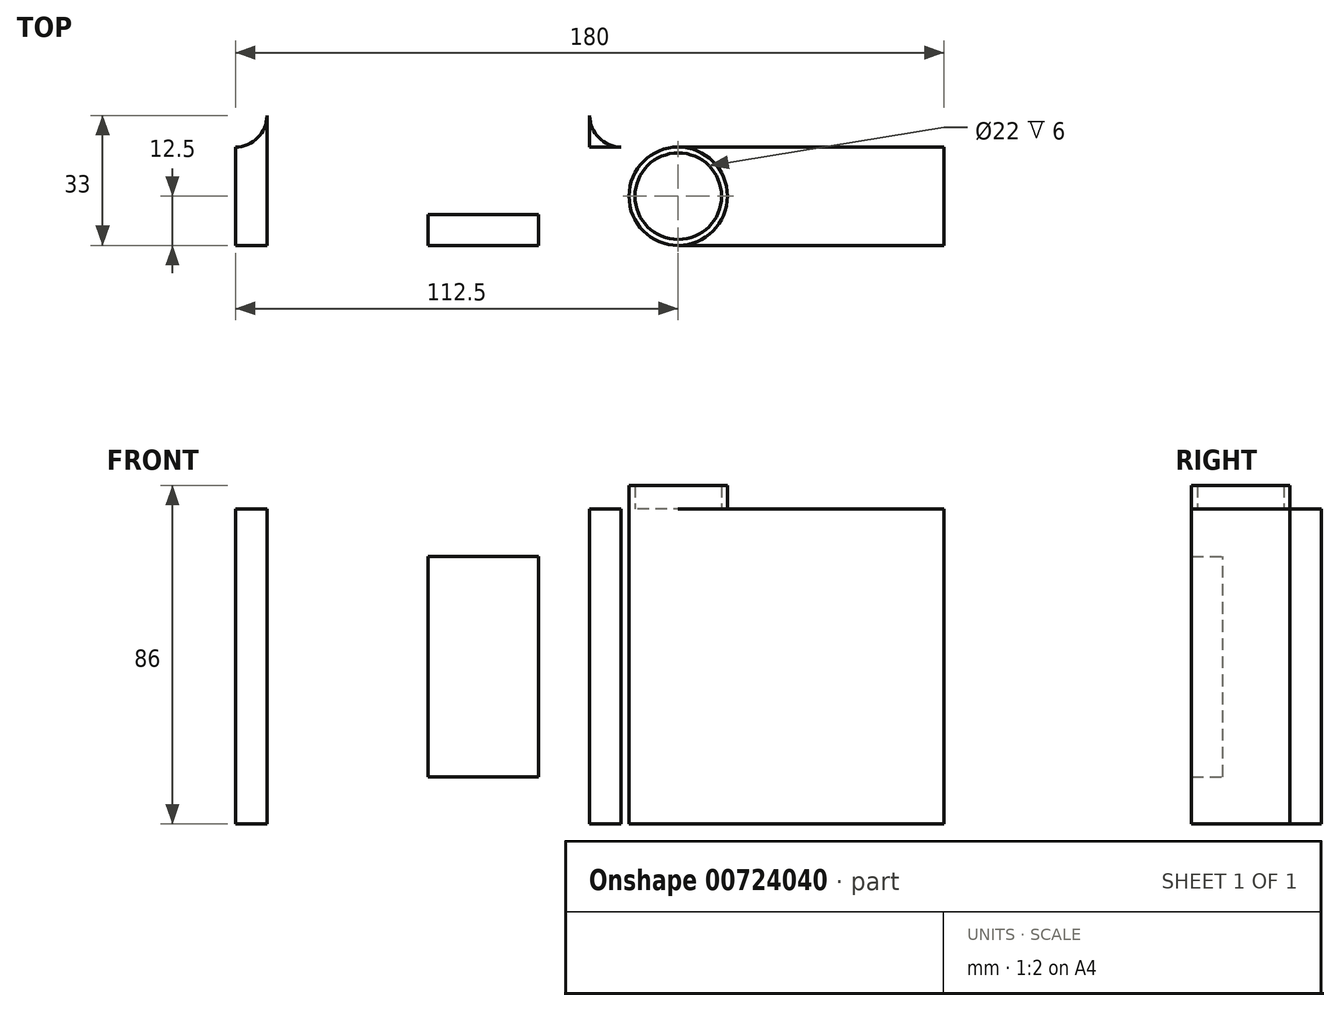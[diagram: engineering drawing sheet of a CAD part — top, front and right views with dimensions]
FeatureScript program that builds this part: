
annotation { "Feature Type Name" : "Feature", "Feature Type Description" : "" }
export const myFeature = defineFeature(function(context is Context, id is Id, definition is map)
    precondition{}
    {
        {
            var Q0;
            Q0=qCreatedBy(makeId("Top.planeOp"),FACE);
            var sketch = newSketch(context, id + "F0", { "sketchPlane" : qUnion([Q0])});
            skLineSegment(sketch, "E0", {"start": v(0, 0) * mm, "end": v(41, 0) * mm});
            skLineSegment(sketch, "E1", {"start": v(0, 0) * mm, "end": v(-49, 0) * mm});
            skLineSegment(sketch, "E2", {"start": v(-49, 0) * mm, "end": v(-49, -15) * mm});
            skLineSegment(sketch, "E3", {"start": v(-49, 0) * mm, "end": v(-49, 19.9) * mm});
            skLineSegment(sketch, "E4", {"start": v(-49, 19.9) * mm, "end": v(0, 19.9) * mm});
            skLineSegment(sketch, "E5", {"start": v(0, 19.9) * mm, "end": v(41, 19.9) * mm});
            skLineSegment(sketch, "E6", {"start": v(41, 19.9) * mm, "end": v(41, 18) * mm});
            skLineSegment(sketch, "E7", {"start": v(-49, -15) * mm, "end": v(0, -15) * mm});
            skLineSegment(sketch, "E8", {"start": v(0, -15) * mm, "end": v(41, -15) * mm});
            skLineSegment(sketch, "E9", {"start": v(41, -15) * mm, "end": v(41, 0) * mm});
            skLineSegment(sketch, "E10", {"start": v(41, -15) * mm, "end": v(131, -15) * mm});
            skLineSegment(sketch, "E11", {"start": v(41, -15) * mm, "end": v(41, 10) * mm});
            skLineSegment(sketch, "E12", {"start": v(41, 10) * mm, "end": v(131, 10) * mm});
            skLineSegment(sketch, "E13", {"start": v(131, 10) * mm, "end": v(131, -15) * mm});
            skLineSegment(sketch, "E14", {"start": v(42.9, 10) * mm, "end": v(41, 10) * mm});
            skLineSegment(sketch, "E15", {"start": v(-49, 19.9) * mm, "end": v(-49, 9.95) * mm});
            skLineSegment(sketch, "E16", {"start": v(-49, 19.9) * mm, "end": v(-49, 10) * mm});
            skLineSegment(sketch, "E17", {"start": v(-49, 10) * mm, "end": v(-49, 10) * mm});
            skLineSegment(sketch, "E18", {"start": v(-41, 18) * mm, "end": v(-41, 19.9) * mm});
            skLineSegment(sketch, "E19", {"start": v(24, 19.9) * mm, "end": v(24, 19.9) * mm});
            skPoint(sketch, "E20.visualSharp", {"position": v(-41, 10) * mm});
            skArc(sketch, "E20.filletArc", {"start": v(-49, 10) * mm, "mid": v(-43.34, 12.34) * mm, "end": v(-41, 18) * mm});
            skLineSegment(sketch, "E21", {"start": v(41, -15) * mm, "end": v(86, -15) * mm});
            skLineSegment(sketch, "E22", {"start": v(86, -15) * mm, "end": v(86, 10) * mm});
            skLineSegment(sketch, "E23", {"start": v(86, 10) * mm, "end": v(86, -2.5) * mm});
            skLineSegment(sketch, "E24", {"start": v(41, -15) * mm, "end": v(63.5, -15) * mm});
            skLineSegment(sketch, "E25", {"start": v(63.5, -15) * mm, "end": v(63.5, 10) * mm});
            skLineSegment(sketch, "E26", {"start": v(63.5, 10) * mm, "end": v(63.5, -2.5) * mm});
            skCircle(sketch, "E27", {"center": v(63.5, -2.5) * mm, "radius": 12.5 * mm});
            skCircle(sketch, "E28", {"center": v(63.5, -2.5) * mm, "radius": 11 * mm});
            skLineSegment(sketch, "E29", {"start": v(49, 10) * mm, "end": v(49, 10) * mm});
            skPoint(sketch, "E30.newPointA", {"position": v(41, 10) * mm});
            skArc(sketch, "E30.filletArc", {"start": v(41, 18) * mm, "mid": v(43.34, 12.34) * mm, "end": v(49, 10) * mm});
            skSolve(sketch);
        }
        {
            var Q0;
            {var subQ13=sQuery(id+"F0.wireOp",EDGE,"E0");Q0=makeQuery(id+"F0.imprint","IMPRINT",FACE,{"disambiguationData":[TD([[makeQuery(id+"F0.imprint","IMPRINT",EDGE,{"derivedFrom":subQ13}),1.0]])]});}
            var Q1;
            {var subQ1=sQuery(id+"F0.wireOp",EDGE,"E0");Q1=makeQuery(id+"F0.imprint","IMPRINT",FACE,{"disambiguationData":[TD([[makeQuery(id+"F0.imprint","IMPRINT",EDGE,{"derivedFrom":subQ1}),-1.0]])]});}
            var Q2;
            {var subQ0=sQuery(id+"F0.wireOp",EDGE,"E14");Q2=makeQuery(id+"F0.imprint","IMPRINT",FACE,{"disambiguationData":[TD([[makeQuery(id+"F0.imprint","IMPRINT",EDGE,{"derivedFrom":subQ0}),1.0]])]});}
            var Q3;
            {var subQ1=sQuery(id+"F0.wireOp",EDGE,"E21");Q3=makeQuery(id+"F0.imprint","IMPRINT",FACE,{"disambiguationData":[TD([[makeQuery(id+"F0.imprint","IMPRINT",EDGE,{"derivedFrom":subQ1}),1.0]])]});}
            var Q4;
            Q4=makeQuery(id+"F0.imprint","IMPRINT",FACE,{"disambiguationData":[TD([[makeQuery(id+"F0.imprint","IMPRINT",EDGE,{"derivedFrom":sQuery(id+"F0.wireOp",EDGE,"E10")}),1.0]])]});
            var Q5;
            {var subQ0=sQuery(id+"F0.wireOp",EDGE,"E26");var subQ1=sQuery(id+"F0.wireOp",EDGE,"E25");var subQ2=makeQuery(id+"F0.imprint","INTERSECT",VERTEX,{"derivedFrom":[subQ1,subQ0]});Q5=makeQuery(id+"F0.imprint","IMPRINT",FACE,{"disambiguationData":[TD([[makeQuery(id+"F0.imprint","IMPRINT",EDGE,{"disambiguationData":[TD([[subQ2,1.0]])],"derivedFrom":subQ1}),-1.0]])]});}
            var Q6;
            {var subQ0=sQuery(id+"F0.wireOp",EDGE,"E26");var subQ1=sQuery(id+"F0.wireOp",EDGE,"E25");var subQ2=makeQuery(id+"F0.imprint","INTERSECT",VERTEX,{"derivedFrom":[subQ1,subQ0]});Q6=makeQuery(id+"F0.imprint","IMPRINT",FACE,{"disambiguationData":[TD([[makeQuery(id+"F0.imprint","IMPRINT",EDGE,{"disambiguationData":[TD([[subQ2,1.0]])],"derivedFrom":subQ1}),1.0]])]});}
            var Q7;
            {var subQ1=sQuery(id+"F0.wireOp",EDGE,"E25");var subQ3=sQuery(id+"F0.wireOp",EDGE,"E28");var subQ4=makeQuery(id+"F0.imprint","INTERSECT",VERTEX,{"derivedFrom":[subQ1,subQ3]});Q7=makeQuery(id+"F0.imprint","IMPRINT",FACE,{"disambiguationData":[TD([[makeQuery(id+"F0.imprint","IMPRINT",EDGE,{"disambiguationData":[TD([[subQ4,1.0]])],"derivedFrom":subQ3}),-1.0]])]});}
            var Q8;
            {var subQ1=sQuery(id+"F0.wireOp",EDGE,"E25");var subQ3=sQuery(id+"F0.wireOp",EDGE,"E28");var subQ4=makeQuery(id+"F0.imprint","INTERSECT",VERTEX,{"derivedFrom":[subQ1,subQ3]});Q8=makeQuery(id+"F0.imprint","IMPRINT",FACE,{"disambiguationData":[TD([[makeQuery(id+"F0.imprint","IMPRINT",EDGE,{"disambiguationData":[TD([[subQ4,-1.0]])],"derivedFrom":subQ3}),-1.0]])]});}
            extrude(context, id + "F1", {"entities" : qUnion([Q0, Q1, Q2, Q3, Q4, Q5, Q6, Q7, Q8]), "endBound" : BoundingType.SYMMETRIC, "depth" : 80 * mm, "offsetDistance" : 25 * mm});
        }
        {
            var Q0;
            {var subQ1=sQuery(id+"F0.wireOp",EDGE,"E25");var subQ3=sQuery(id+"F0.wireOp",EDGE,"E28");var subQ4=makeQuery(id+"F0.imprint","INTERSECT",VERTEX,{"derivedFrom":[subQ1,subQ3]});Q0=makeQuery(id+"F0.imprint","IMPRINT",FACE,{"disambiguationData":[TD([[makeQuery(id+"F0.imprint","IMPRINT",EDGE,{"disambiguationData":[TD([[subQ4,1.0]])],"derivedFrom":subQ3}),-1.0]])]});}
            var Q1;
            {var subQ1=sQuery(id+"F0.wireOp",EDGE,"E25");var subQ3=sQuery(id+"F0.wireOp",EDGE,"E28");var subQ4=makeQuery(id+"F0.imprint","INTERSECT",VERTEX,{"derivedFrom":[subQ1,subQ3]});Q1=makeQuery(id+"F0.imprint","IMPRINT",FACE,{"disambiguationData":[TD([[makeQuery(id+"F0.imprint","IMPRINT",EDGE,{"disambiguationData":[TD([[subQ4,-1.0]])],"derivedFrom":subQ3}),-1.0]])]});}
            extrude(context, id + "F2", {"entities" : qUnion([Q0, Q1]), "operationType" : NewBodyOperationType.ADD, "depth" : 46 * mm, "offsetDistance" : 25 * mm});
        }
        {
            var Q0;
            Q0=makeQuery(id+"F1.opExtrude","SWEPT_FACE",FACE,{"disambiguationData":[OSD([sQuery(id+"F0.wireOp",EDGE,"E4"),sQuery(id+"F0.wireOp",EDGE,"E5"),sQuery(id+"F0.wireOp",EDGE,"xz5f9xwi-Rsmr-XxTJ-q0zS-7Ez9dwEFxO9i"),sQuery(id+"F0.wireOp",EDGE,"bfca25d2-a378-4aca-a1b2-c8aff88f09880.MirrorCS")])]});
            var sketch = newSketch(context, id + "F3", { "sketchPlane" : qUnion([Q0])});
            skLineSegment(sketch, "E31", {"start": v(0, 0) * mm, "end": v(30, 0) * mm});
            skLineSegment(sketch, "E32", {"start": v(0, 0) * mm, "end": v(-33, 0) * mm});
            skPoint(sketch, "E32.endSnap0", {"position": v(-41, 0) * mm});
            skLineSegment(sketch, "E33", {"start": v(0, 0) * mm, "end": v(0, 33) * mm});
            skPoint(sketch, "E33.endSnap0", {"position": v(0, 40) * mm});
            skLineSegment(sketch, "E34", {"start": v(0, 0) * mm, "end": v(0, -30) * mm});
            skLineSegment(sketch, "E35", {"start": v(-33, 0) * mm, "end": v(-33, 33) * mm});
            skLineSegment(sketch, "E36", {"start": v(-33, 33) * mm, "end": v(0, 33) * mm});
            skLineSegment(sketch, "E37.MirrorCS", {"start": v(33, 33) * mm, "end": v(0, 33) * mm});
            skLineSegment(sketch, "E38.MirrorCS", {"start": v(33, 0) * mm, "end": v(33, 33) * mm});
            skLineSegment(sketch, "E39.MirrorCS", {"start": v(-33, 0) * mm, "end": v(-33, -33) * mm});
            skLineSegment(sketch, "E40.MirrorCS", {"start": v(-33, -33) * mm, "end": v(0, -33) * mm});
            skLineSegment(sketch, "E41.MirrorCS", {"start": v(33, -33) * mm, "end": v(0, -33) * mm});
            skLineSegment(sketch, "E42.MirrorCS", {"start": v(33, 0) * mm, "end": v(33, -33) * mm});
            skLineSegment(sketch, "E43", {"start": v(0, 0) * mm, "end": v(-28, 0) * mm});
            skLineSegment(sketch, "E44", {"start": v(0, 0) * mm, "end": v(0, 28) * mm});
            skLineSegment(sketch, "E45", {"start": v(-28, 0) * mm, "end": v(-28, 28) * mm});
            skLineSegment(sketch, "E46", {"start": v(-28, 28) * mm, "end": v(0, 28) * mm});
            skLineSegment(sketch, "E47.MirrorCS", {"start": v(28, 0) * mm, "end": v(28, 28) * mm});
            skLineSegment(sketch, "E48.MirrorCS", {"start": v(28, 28) * mm, "end": v(0, 28) * mm});
            skLineSegment(sketch, "E49.MirrorCS", {"start": v(-28, -28) * mm, "end": v(0, -28) * mm});
            skLineSegment(sketch, "E50.MirrorCS", {"start": v(-28, 0) * mm, "end": v(-28, -28) * mm});
            skLineSegment(sketch, "E51.MirrorCS", {"start": v(28, -28) * mm, "end": v(0, -28) * mm});
            skLineSegment(sketch, "E52.MirrorCS", {"start": v(28, 0) * mm, "end": v(28, -28) * mm});
            skSolve(sketch);
        }
        {
            var Q0;
            Q0=makeQuery(id+"F3.imprint","IMPRINT",FACE,{"disambiguationData":[TD([[makeQuery(id+"F3.imprint","IMPRINT",EDGE,{"derivedFrom":sQuery(id+"F3.wireOp",EDGE,"E32")}),-1.0]])]});
            var Q1;
            Q1=makeQuery(id+"F3.imprint","IMPRINT",FACE,{"disambiguationData":[TD([[makeQuery(id+"F3.imprint","IMPRINT",EDGE,{"derivedFrom":sQuery(id+"F3.wireOp",EDGE,"E32")}),1.0]])]});
            extrude(context, id + "F4", {"entities" : qUnion([Q0, Q1]), "operationType" : NewBodyOperationType.REMOVE, "oppositeDirection" : true, "depth" : 27 * mm, "offsetDistance" : 25 * mm});
        }
        {
            var Q0;
            Q0=makeQuery(id+"F4.boolean.opBoolean","SPLIT",FACE,{"disambiguationData":[TD([makeQuery(id+"F4.opExtrude","SWEPT_FACE",FACE,{"disambiguationData":[OSD([sQuery(id+"F3.wireOp",EDGE,"E45"),sQuery(id+"F3.wireOp",EDGE,"E50.MirrorCS")])]})])],"derivedFrom":makeQuery(id+"F1.opExtrude","SWEPT_FACE",FACE,{"disambiguationData":[OSD([sQuery(id+"F0.wireOp",EDGE,"E4"),sQuery(id+"F0.wireOp",EDGE,"E5")])]})});
            extrude(context, id + "F5", {"entities" : qUnion([Q0]), "operationType" : NewBodyOperationType.REMOVE, "oppositeDirection" : true, "depth" : 60.6 * mm, "offsetDistance" : 25 * mm});
        }
    });
